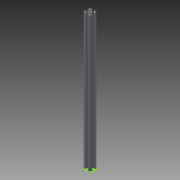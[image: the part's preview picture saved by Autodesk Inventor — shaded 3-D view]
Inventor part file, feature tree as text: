
AUTODESK INVENTOR PART (.ipt)
format: ipt  version: 2017 (Build 210142000, 142)  size: 335,872 bytes
history: native  units: mm
features: sketch x2, extrude x1, plane x1
ambient origin geometry x8: Origin, YZ Plane, XZ Plane, XY Plane, X Axis, Y Axis, Z Axis, Center Point
bodies: Solid1 (feature_tree)
feature tree (4):
  sketch  "Sketch1"  dims[d0=600.0mm d1=0.0mm]
  extrude  "Extrusion1"  [1 undecoded]
  plane  "Work Plane1"
  sketch  "Sketch3"
note: 1 required parameter value undecoded (feature->parameter linkage not recoverable at this tier; creation-order binding heuristic only, values carry confidence <= 0.55)
